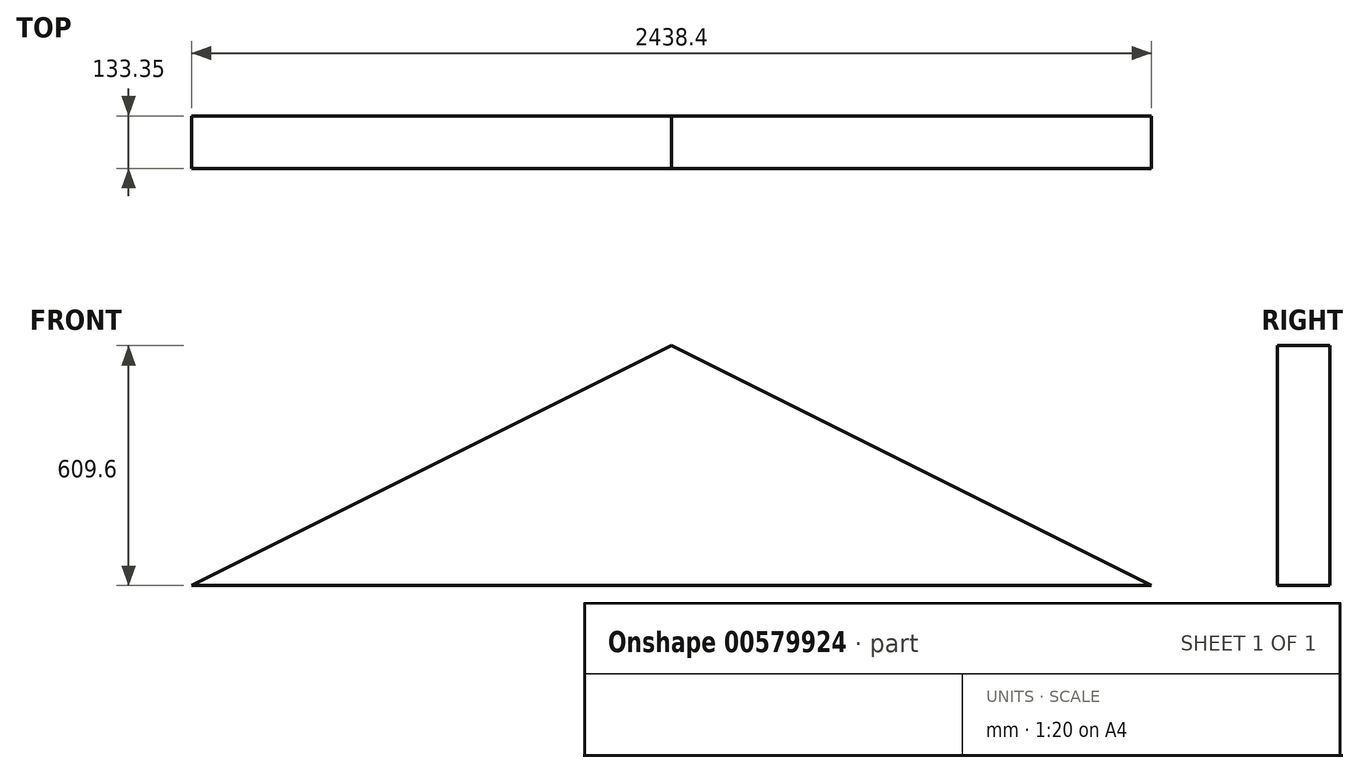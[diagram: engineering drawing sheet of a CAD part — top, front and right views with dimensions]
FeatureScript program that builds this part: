
annotation { "Feature Type Name" : "Feature", "Feature Type Description" : "" }
export const myFeature = defineFeature(function(context is Context, id is Id, definition is map)
    precondition{}
    {
        {
            var Q0;
            Q0=qCreatedBy(makeId("Front.planeOp"),FACE);
            var sketch = newSketch(context, id + "F0", { "sketchPlane" : qUnion([Q0])});
            skLineSegment(sketch, "E0", {"start": v(-1338.67, -3.08) * mm, "end": v(1099.73, -3.08) * mm});
            skLineSegment(sketch, "E1", {"start": v(-1338.67, -3.08) * mm, "end": v(-119.47, 606.52) * mm});
            skLineSegment(sketch, "E2", {"start": v(-119.47, 606.52) * mm, "end": v(1099.73, -3.08) * mm});
            skPoint(sketch, "E3.start.orphan", {"position": v(-119.47, -3.08) * mm});
            skSolve(sketch);
        }
        {
            var Q0;
            Q0 = qSketchRegion(id + "F0", true);
            extrude(context, id + "F1", {"entities" : qUnion([Q0]), "depth" : 133.35 * mm, "offsetDistance" : 25.4 * mm});
        }
    });
